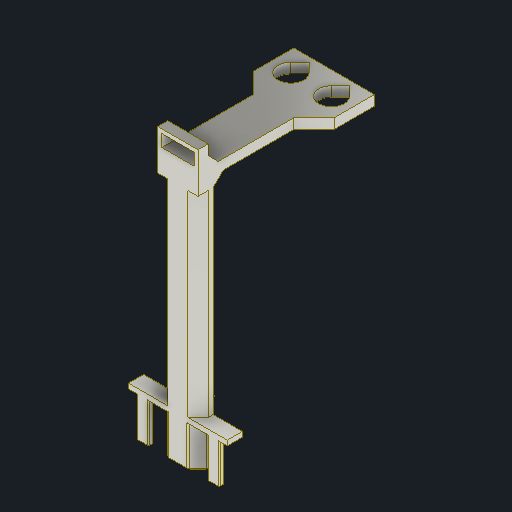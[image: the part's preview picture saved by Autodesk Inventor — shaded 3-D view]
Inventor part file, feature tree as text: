
AUTODESK INVENTOR PART (.ipt)
format: ipt  version: 2022 (Build 260153000, 153)  size: 724,480 bytes
history: native  units: in
note: dims shown in document units (in); Inventor stores cm internally (conversion verified against a paired STEP export)
features: sketch x17, extrude x15, projected_geometry x9, chamfer x7, reference x5, other x4, fillet x1
ambient origin geometry x8: Origin, YZ Plane, XZ Plane, XY Plane, X Axis, Y Axis, Z Axis, Center Point
bodies: Solid1 (feature_tree)
feature tree (58):
  extrude  "Extrusion1"  Depth=6.5in
  extrude  "Extrusion2"  Depth=1.031in
  extrude  "Extrusion3"  Depth=0.25in TaperAngle=0.0deg
  chamfer  "Chamfer1"  Distance=0.25in
  extrude  "Extrusion5"  Depth=0.025in
  extrude  "Extrusion6"  Depth=0.025in
  extrude  "Extrusion7"  Depth=0.1in
  extrude  "Extrusion8"  Depth=0.495in
  sketch  "Sketch9"  dims[d33=0.4936in d34=0.25in d35=3.5in d36=0.0in]
  extrude  "Extrusion9"  Depth=0.25in
  chamfer  "Chamfer6"  Distance=3.5in
  extrude  "Extrusion10"  Depth=0.5in TaperAngle=0.0deg
  extrude  "Extrusion12"  Depth=0.25in
  extrude  "Extrusion13"  Depth=0.5in
  fillet  "Fillet1"  Radius=0.176in
  sketch  "Sketch14"  dims[d51=0.32in d52=0.64in]
  extrude  "Extrusion14"  Depth=0.32in
  extrude  "Extrusion15"  Depth=1.0in
  chamfer  "Chamfer11"  Distance=0.25in
  chamfer  "Chamfer12"  Distance=0.25in Angle=45.0deg
  chamfer  "Chamfer13"  Distance=1.0in
  sketch  "Sketch20"  dims[d85=0.125in d86=0.2in]
  extrude  "Extrusion18"  Depth=0.125in
  chamfer  "Chamfer14"  Distance=0.125in
  extrude  "Extrusion20"  Depth=0.2in
  chamfer  "Chamfer17"  Distance=1.0in
  sketch  "Sketch1"  dims[d0=1.0in d1=6.5in]
  sketch  "Sketch2"  dims[d2=0.495in d3=1.031in]
  projected_geometry  "Projected Loop1"
  sketch  "Sketch3"  dims[d4=0.125in d5=0.0in d6=0.25in d7=0.125in d8=0.0in d9=0.0in d10=0.25in d11=0.0in]
  projected_geometry  "Projected Loop2"
  sketch  "Sketch5"  dims[d12=0.25in d13=0.125in d14=45.0deg d25=0.025in]
  reference  "Reference1"
  reference  "Reference2"
  reference  "Reference3"
  sketch  "Sketch6"  dims[d26=0.05in d27=0.025in]
  projected_geometry  "Projected Loop3"
  sketch  "Sketch7"  dims[d28=0.05in d29=0.1in]
  sketch  "Sketch8"  dims[d30=0.5in d31=0.0in d32=0.495in]
  reference  "Reference4"
  reference  "Reference5"
  sketch  "Sketch10"  dims[d37=1.0in d38=0.5in d39=0.0in]
  projected_geometry  "Projected Loop4"
  sketch  "Sketch12"  dims[d40=1.0in d41=0.25in]
  projected_geometry  "Projected Loop5"
  sketch  "Sketch13"  dims[d42=0.5in d43=0.0in d49=1.0079in d50=0.176in]
  projected_geometry  "Projected Loop6"
  projected_geometry  "Projected Loop7"
  sketch  "Sketch15"  dims[d53=0.496in d54=0.64in d55=0.25in d56=0.0in d60=0.25in d61=0.125in d62=45.0deg d63=1.0in d64=0.0in]
  sketch  "Sketch16"  dims[d74=1.225in d75=1.225in d76=0.125in d77=0.0in]
  projected_geometry  "Projected Loop8"
  projected_geometry  "Projected Loop9"
  sketch  "Sketch21"  dims[d87=0.495in d88=1.0in d89=0.0in]
  sketch  "Sketch23"  dims[d90=0.125in d91=0.125in d92=0.2in d93=0.5in d94=0.125in d95=0.0in d96=0.125in d97=0.0in d107=0.025in d108=0.125in d109=45.0deg d110=0.025in d111=0.125in d112=45.0deg d113=0.025in d114=0.125in d115=45.0deg d125=0.2in d126=0.0in d127=0.5in d128=0.125in d129=45.0deg d138=0.5in d139=0.1in d140=0.25in d141=0.0in d142=0.25in d143=0.125in d144=45.0deg d123=0.5in d124=0.0344in]
  parser-record x1  (decoder bookkeeping rows leaked as tree rows — omitted from the tree; the rows remain in map.json)
  other  "Prototype Assembly.iam"
  other  "Base:1"
  other  "hc-sr04:1"
note: 1 file-system path scrubbed to <path> (originals preserved in map.json)
